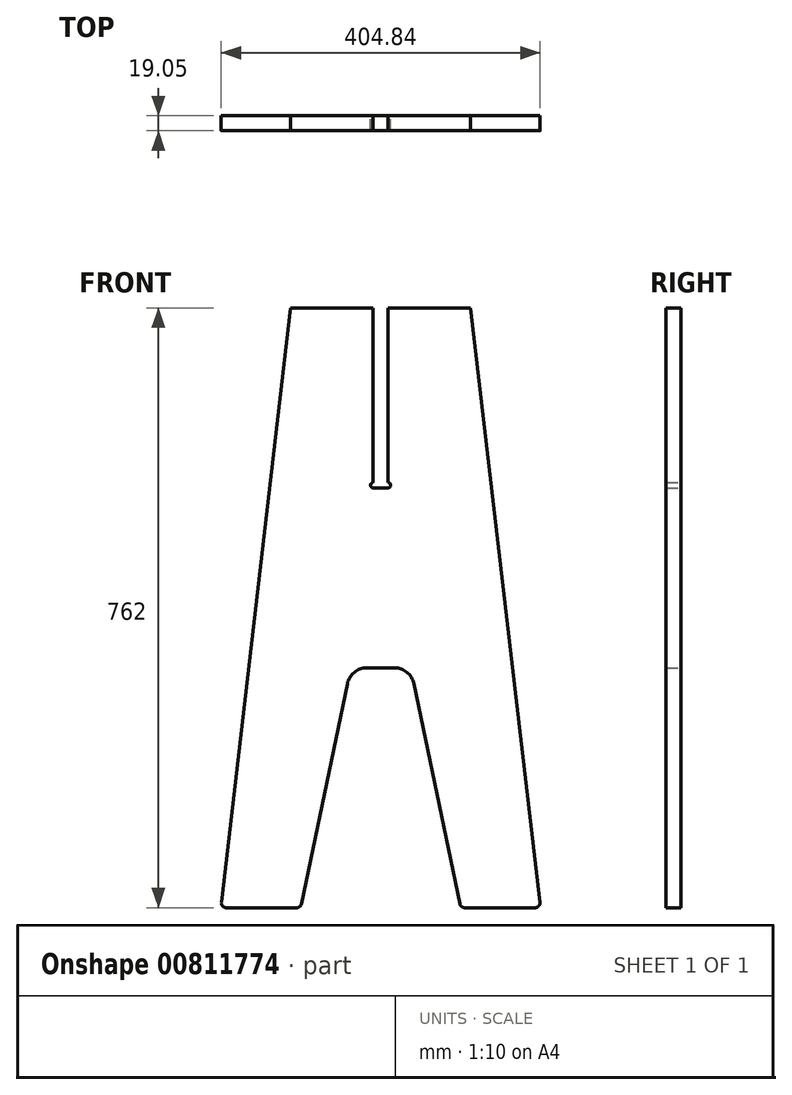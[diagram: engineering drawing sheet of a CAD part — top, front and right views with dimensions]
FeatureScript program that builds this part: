
annotation { "Feature Type Name" : "Feature", "Feature Type Description" : "" }
export const myFeature = defineFeature(function(context is Context, id is Id, definition is map)
    precondition{}
    {
        {
            var Q0;
            Q0=qCreatedBy(makeId("Front.planeOp"),FACE);
            var sketch = newSketch(context, id + "F0", { "sketchPlane" : qUnion([Q0])});
            skLineSegment(sketch, "E0", {"start": v(-202.37, -297.71) * mm, "end": v(-114.3, 457.2) * mm});
            skLineSegment(sketch, "E1", {"start": v(-114.3, 457.2) * mm, "end": v(-9.53, 457.2) * mm});
            skLineSegment(sketch, "E2", {"start": v(-9.53, 457.2) * mm, "end": v(-9.53, 235.2) * mm});
            skLineSegment(sketch, "E3", {"start": v(-9.53, 228.6) * mm, "end": v(9.53, 228.6) * mm});
            skLineSegment(sketch, "E4", {"start": v(9.52, 457.2) * mm, "end": v(114.3, 457.2) * mm});
            skLineSegment(sketch, "E5", {"start": v(114.3, 457.2) * mm, "end": v(202.37, -297.71) * mm});
            skLineSegment(sketch, "E6", {"start": v(196.07, -304.8) * mm, "end": v(106.76, -304.8) * mm});
            skLineSegment(sketch, "E7", {"start": v(100.55, -299.75) * mm, "end": v(42.31, -20.22) * mm});
            skLineSegment(sketch, "E8", {"start": v(17.45, 0) * mm, "end": v(-17.45, 0) * mm});
            skLineSegment(sketch, "E9", {"start": v(-42.31, -20.22) * mm, "end": v(-100.55, -299.75) * mm});
            skLineSegment(sketch, "E10", {"start": v(-106.76, -304.8) * mm, "end": v(-196.07, -304.8) * mm});
            skLineSegment(sketch, "E11", {"start": v(0, 228.6) * mm, "end": v(0, 0) * mm, "construction": true});
            skPoint(sketch, "E12.visualSharp", {"position": v(-203.2, -304.8) * mm});
            skArc(sketch, "E12.filletArc", {"start": v(-202.37, -297.71) * mm, "mid": v(-200.8, -302.67) * mm, "end": v(-196.07, -304.8) * mm});
            skPoint(sketch, "E13.visualSharp", {"position": v(-101.6, -304.8) * mm});
            skArc(sketch, "E13.filletArc", {"start": v(-106.76, -304.8) * mm, "mid": v(-102.76, -303.38) * mm, "end": v(-100.55, -299.75) * mm});
            skPoint(sketch, "E14.visualSharp", {"position": v(101.6, -304.8) * mm});
            skArc(sketch, "E14.filletArc", {"start": v(100.55, -299.75) * mm, "mid": v(102.76, -303.38) * mm, "end": v(106.76, -304.8) * mm});
            skPoint(sketch, "E15.visualSharp", {"position": v(203.2, -304.8) * mm});
            skArc(sketch, "E15.filletArc", {"start": v(196.07, -304.8) * mm, "mid": v(200.8, -302.67) * mm, "end": v(202.37, -297.71) * mm});
            skPoint(sketch, "E16.visualSharp", {"position": v(-38.1, 0) * mm});
            skArc(sketch, "E16.filletArc", {"start": v(-17.45, 0) * mm, "mid": v(-33.47, -5.7) * mm, "end": v(-42.31, -20.22) * mm});
            skPoint(sketch, "E17.visualSharp", {"position": v(38.1, 0) * mm});
            skArc(sketch, "E17.filletArc", {"start": v(42.31, -20.22) * mm, "mid": v(33.47, -5.7) * mm, "end": v(17.45, 0) * mm});
            skArc(sketch, "E18", {"start": v(-9.53, 235.2) * mm, "mid": v(-12.83, 231.9) * mm, "end": v(-9.53, 228.6) * mm});
            skArc(sketch, "E19", {"start": v(9.53, 228.6) * mm, "mid": v(12.83, 231.9) * mm, "end": v(9.53, 235.2) * mm});
            skLineSegment(sketch, "E20.trimOffspring", {"start": v(9.53, 235.2) * mm, "end": v(9.52, 457.2) * mm});
            skSolve(sketch);
        }
        {
            var Q0;
            Q0=makeQuery(id+"F0.imprint","IMPRINT",FACE,{"disambiguationData":[TD([[makeQuery(id+"F0.imprint","IMPRINT",EDGE,{"derivedFrom":sQuery(id+"F0.wireOp",EDGE,"E0")}),-1.0]])]});
            extrude(context, id + "F1", {"entities" : qUnion([Q0]), "depth" : 19.05 * mm, "offsetDistance" : 25.4 * mm});
        }
    });
